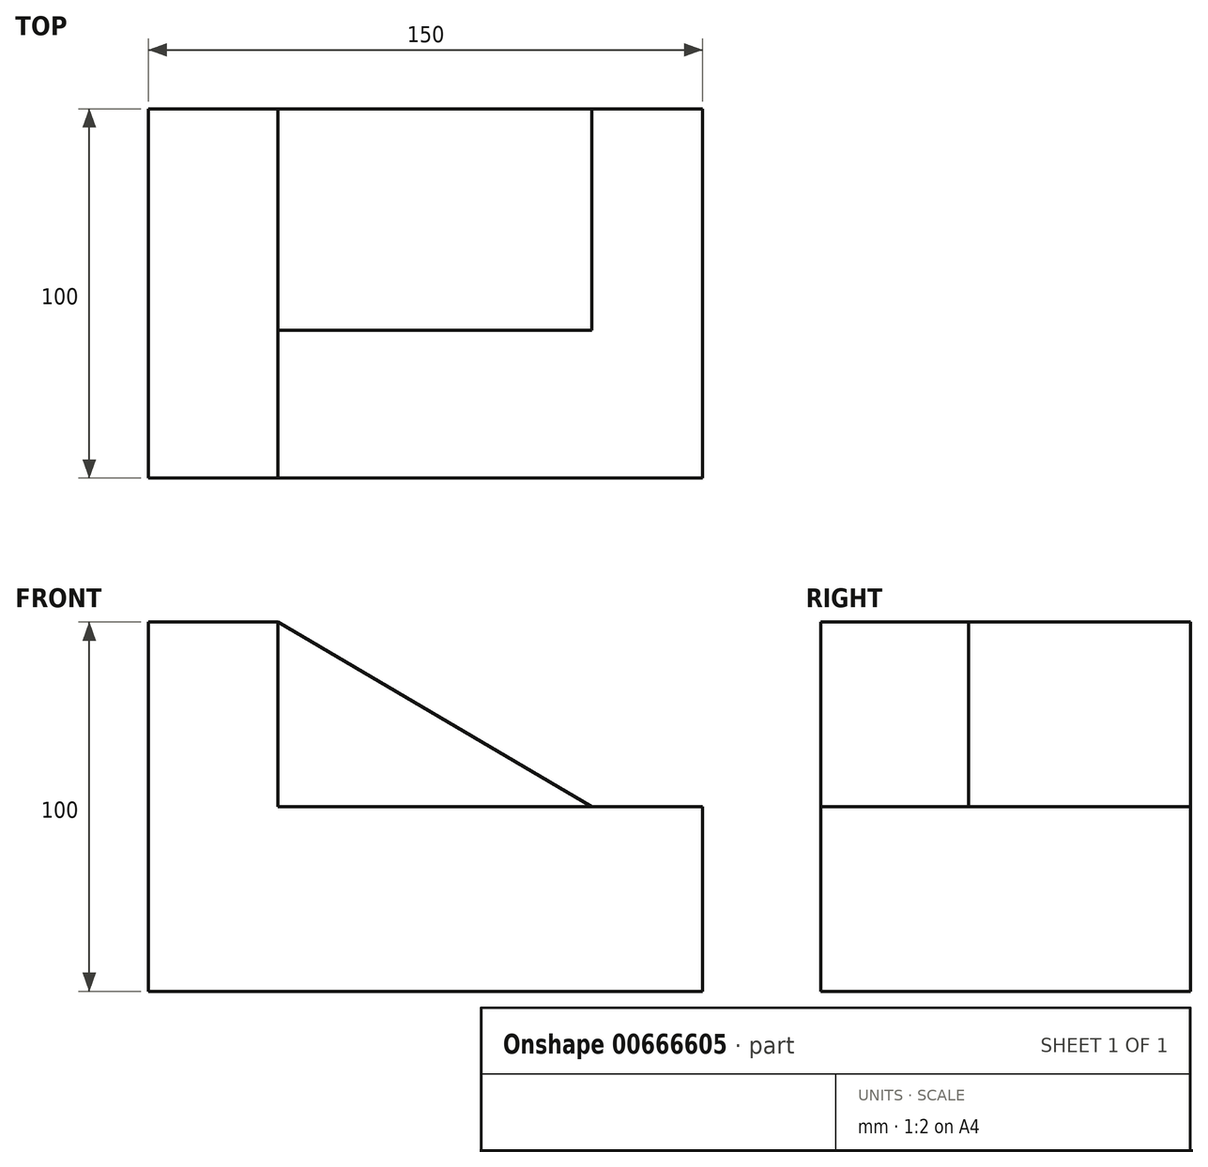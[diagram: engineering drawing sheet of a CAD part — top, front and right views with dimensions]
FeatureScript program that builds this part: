
annotation { "Feature Type Name" : "Feature", "Feature Type Description" : "" }
export const myFeature = defineFeature(function(context is Context, id is Id, definition is map)
    precondition{}
    {
        {
            var Q0;
            Q0=qCreatedBy(makeId("Top.planeOp"),FACE);
            var sketch = newSketch(context, id + "F0", { "sketchPlane" : qUnion([Q0])});
            skLineSegment(sketch, "E0.bottom", {"start": v(-59.33, 46.74) * mm, "end": v(90.67, 46.74) * mm});
            skLineSegment(sketch, "E0.top", {"start": v(-59.33, -53.26) * mm, "end": v(90.67, -53.26) * mm});
            skLineSegment(sketch, "E0.left", {"start": v(-59.33, 46.74) * mm, "end": v(-59.33, -53.26) * mm});
            skLineSegment(sketch, "E0.right", {"start": v(90.67, 46.74) * mm, "end": v(90.67, -53.26) * mm});
            skSolve(sketch);
        }
        {
            var Q0;
            Q0=makeQuery(id+"F0.imprint","IMPRINT",FACE,{"disambiguationData":[TD([[makeQuery(id+"F0.imprint","IMPRINT",EDGE,{"derivedFrom":sQuery(id+"F0.wireOp",EDGE,"E0.bottom")}),-1.0]])]});
            extrude(context, id + "F1", {"entities" : qUnion([Q0]), "depth" : 50 * mm, "offsetDistance" : 25 * mm});
        }
        {
            var Q0;
            Q0=makeQuery(id+"F1.opExtrude","CAP_FACE",FACE,{"disambiguationData":[OSD([sQuery(id+"F0.wireOp",EDGE,"E0.bottom"),sQuery(id+"F0.wireOp",EDGE,"E0.top"),sQuery(id+"F0.wireOp",EDGE,"E0.left"),sQuery(id+"F0.wireOp",EDGE,"E0.right")])],"isStart":false});
            var sketch = newSketch(context, id + "F2", { "sketchPlane" : qUnion([Q0])});
            skLineSegment(sketch, "E1.bottom", {"start": v(-59.33, -53.26) * mm, "end": v(-24.33, -53.26) * mm});
            skLineSegment(sketch, "E1.top", {"start": v(-59.33, 46.74) * mm, "end": v(-24.33, 46.74) * mm});
            skLineSegment(sketch, "E1.left", {"start": v(-59.33, -53.26) * mm, "end": v(-59.33, 46.74) * mm});
            skLineSegment(sketch, "E1.right", {"start": v(-24.33, -53.26) * mm, "end": v(-24.33, 46.74) * mm});
            skSolve(sketch);
        }
        {
            var Q0;
            Q0=makeQuery(id+"F2.imprint","IMPRINT",FACE,{"disambiguationData":[TD([[makeQuery(id+"F2.imprint","IMPRINT",EDGE,{"derivedFrom":sQuery(id+"F2.wireOp",EDGE,"E1.bottom")}),1.0]])]});
            extrude(context, id + "F3", {"entities" : qUnion([Q0]), "operationType" : NewBodyOperationType.ADD, "depth" : 50 * mm, "offsetDistance" : 25 * mm});
        }
        {
            var Q0;
            Q0=makeQuery(id+"F1.opExtrude","CAP_FACE",FACE,{"disambiguationData":[OSD([sQuery(id+"F0.wireOp",EDGE,"E0.bottom"),sQuery(id+"F0.wireOp",EDGE,"E0.top"),sQuery(id+"F0.wireOp",EDGE,"E0.left"),sQuery(id+"F0.wireOp",EDGE,"E0.right")])],"isStart":false});
            var sketch = newSketch(context, id + "F4", { "sketchPlane" : qUnion([Q0])});
            skLineSegment(sketch, "E2.bottom", {"start": v(-24.33, 46.74) * mm, "end": v(60.67, 46.74) * mm});
            skLineSegment(sketch, "E2.top", {"start": v(-24.33, -13.26) * mm, "end": v(60.67, -13.26) * mm});
            skLineSegment(sketch, "E2.left", {"start": v(-24.33, 46.74) * mm, "end": v(-24.33, -13.26) * mm});
            skLineSegment(sketch, "E2.right", {"start": v(60.67, 46.74) * mm, "end": v(60.67, -13.26) * mm});
            skSolve(sketch);
        }
        {
            var Q0;
            Q0=makeQuery(id+"F4.imprint","IMPRINT",FACE,{"disambiguationData":[TD([[makeQuery(id+"F4.imprint","IMPRINT",EDGE,{"derivedFrom":sQuery(id+"F4.wireOp",EDGE,"E2.bottom")}),-1.0]])]});
            extrude(context, id + "F5", {"entities" : qUnion([Q0]), "operationType" : NewBodyOperationType.ADD, "depth" : 50 * mm, "offsetDistance" : 25 * mm});
        }
        {
            var Q0;
            Q0=makeQuery(id+"F5.opExtrude","SWEPT_FACE",FACE,{"disambiguationData":[OSD([sQuery(id+"F4.wireOp",EDGE,"E2.top")])]});
            var sketch = newSketch(context, id + "F6", { "sketchPlane" : qUnion([Q0])});
            skLineSegment(sketch, "E3", {"start": v(-24.33, 100) * mm, "end": v(60.67, 50) * mm});
            skLineSegment(sketch, "E4", {"start": v(60.67, 50) * mm, "end": v(60.67, 100) * mm});
            skLineSegment(sketch, "E5", {"start": v(60.67, 100) * mm, "end": v(-24.33, 100) * mm});
            skSolve(sketch);
        }
        {
            var Q0;
            Q0=makeQuery(id+"F6.imprint","IMPRINT",FACE,{"disambiguationData":[TD([[makeQuery(id+"F6.imprint","IMPRINT",EDGE,{"derivedFrom":sQuery(id+"F6.wireOp",EDGE,"E3")}),1.0]])]});
            extrude(context, id + "F7", {"entities" : qUnion([Q0]), "operationType" : NewBodyOperationType.REMOVE, "oppositeDirection" : true, "depth" : 60 * mm, "offsetDistance" : 25 * mm});
        }
    });
